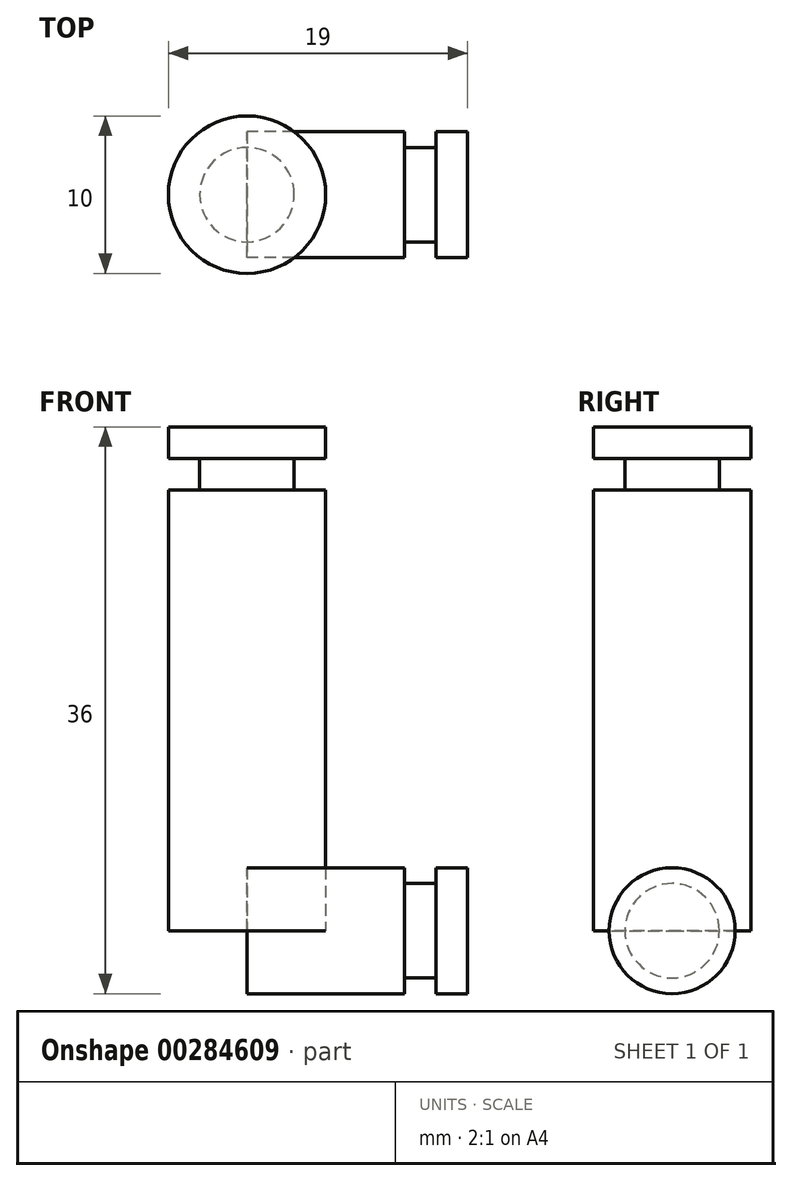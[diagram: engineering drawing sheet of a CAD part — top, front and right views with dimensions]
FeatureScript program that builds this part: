
annotation { "Feature Type Name" : "Feature", "Feature Type Description" : "" }
export const myFeature = defineFeature(function(context is Context, id is Id, definition is map)
    precondition{}
    {
        {
            var Q0;
            Q0=qCreatedBy(makeId("Front.planeOp"),FACE);
            var sketch = newSketch(context, id + "F0", { "sketchPlane" : qUnion([Q0])});
            skLineSegment(sketch, "E0.bottom", {"start": v(0, 0) * mm, "end": v(14, 0) * mm});
            skLineSegment(sketch, "E0.top", {"start": v(0, 4) * mm, "end": v(10, 4) * mm});
            skLineSegment(sketch, "E0.left", {"start": v(0, 0) * mm, "end": v(0, 4) * mm});
            skLineSegment(sketch, "E0.right", {"start": v(14, 0) * mm, "end": v(14, 4) * mm});
            skLineSegment(sketch, "E1.top", {"start": v(10, 3) * mm, "end": v(12, 3) * mm});
            skLineSegment(sketch, "E1.left", {"start": v(10, 4) * mm, "end": v(10, 3) * mm});
            skLineSegment(sketch, "E1.right", {"start": v(12, 4) * mm, "end": v(12, 3) * mm});
            skLineSegment(sketch, "E2.trimOffspring", {"start": v(12, 4) * mm, "end": v(14, 4) * mm});
            skLineSegment(sketch, "E3", {"start": v(-9.1, 0) * mm, "end": v(16.12, 0) * mm, "construction": true});
            skSolve(sketch);
        }
        {
            var Q0;
            Q0 = qSketchRegion(id + "F0", true);
            var Q1;
            Q1=sQuery(id+"F0.wireOp",EDGE,"E3");
            revolve(context, id + "F1", {"entities" : qUnion([Q0]), "axis" : qUnion([Q1]), "revolveType" : RevolveType.FULL});
        }
        {
            var Q0;
            Q0=qCreatedBy(makeId("Front.planeOp"),FACE);
            var sketch = newSketch(context, id + "F2", { "sketchPlane" : qUnion([Q0])});
            skLineSegment(sketch, "E4.bottom", {"start": v(0, 0) * mm, "end": v(-5, 0) * mm});
            skLineSegment(sketch, "E4.top", {"start": v(0, 32) * mm, "end": v(-5, 32) * mm});
            skLineSegment(sketch, "E4.left", {"start": v(0, 0) * mm, "end": v(0, 32) * mm});
            skLineSegment(sketch, "E4.right", {"start": v(-5, 0) * mm, "end": v(-5, 28) * mm});
            skLineSegment(sketch, "E5.bottom", {"start": v(-5, 30) * mm, "end": v(-3, 30) * mm});
            skLineSegment(sketch, "E5.top", {"start": v(-5, 28) * mm, "end": v(-3, 28) * mm});
            skLineSegment(sketch, "E5.right", {"start": v(-3, 30) * mm, "end": v(-3, 28) * mm});
            skLineSegment(sketch, "E6.trimOffspring", {"start": v(-5, 30) * mm, "end": v(-5, 32) * mm});
            skLineSegment(sketch, "E7", {"start": v(0, -8.43) * mm, "end": v(0, 46.98) * mm, "construction": true});
            skSolve(sketch);
        }
        {
            var Q0;
            Q0 = qSketchRegion(id + "F2", true);
            var Q1;
            Q1=sQuery(id+"F2.wireOp",EDGE,"E7");
            revolve(context, id + "F3", {"entities" : qUnion([Q0]), "axis" : qUnion([Q1]), "revolveType" : RevolveType.FULL});
        }
    });
